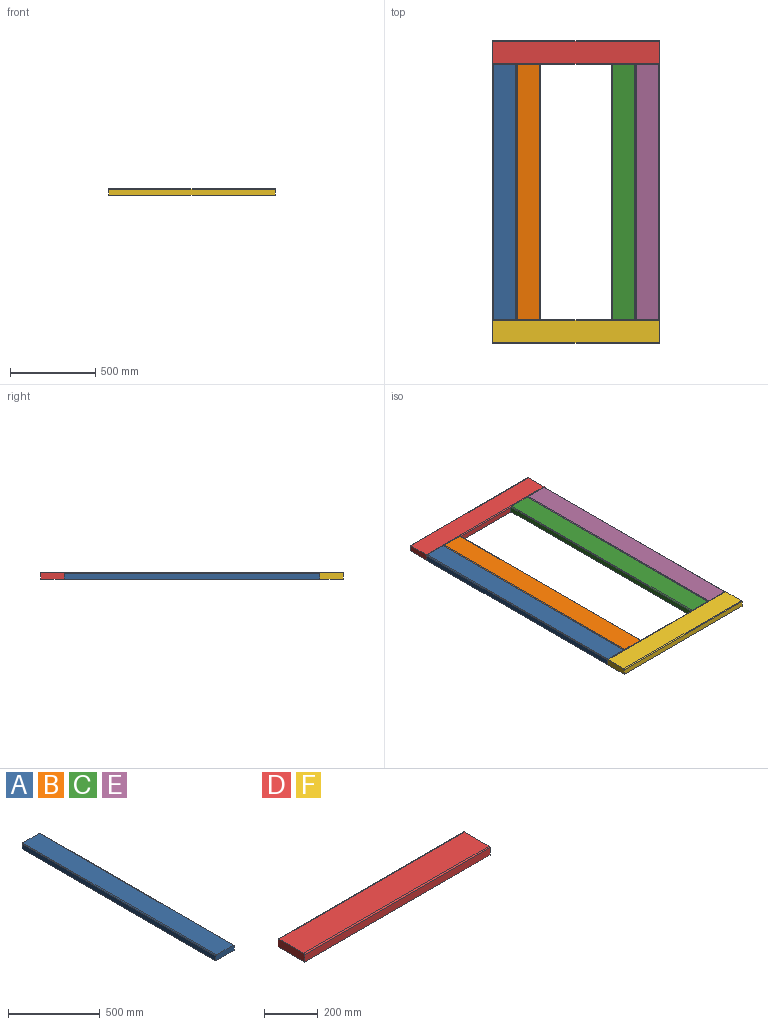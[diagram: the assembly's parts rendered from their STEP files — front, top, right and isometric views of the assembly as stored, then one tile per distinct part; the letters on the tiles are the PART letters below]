
ASSEMBLY  parts=6 mates=15
PART A: 8 faces, bbox 139.7x1498.6x38.1 mm
  f0: plane 1498.6x33.02mm, normal (-1,0,0), area 49483.8mm2, adj f1,f3,f5,f7
  f1: plane 139.7x38.1mm, normal (0,-1,0), area 5311.5mm2, adj f0,f2,f4,f5,f6,f7
  f2: plane 1498.6x33.02mm, normal (1,0,0), area 49483.8mm2, adj f1,f3,f5,f6
  f3: plane 139.7x38.1mm, normal (0,1,0), area 5311.5mm2, adj f0,f2,f4,f5,f6,f7
  f4: plane 1498.6x129.54mm, normal (0,0,1), area 194128.6mm2, adj f1,f3,f6,f7
  f5: plane 1498.6x139.7mm, normal (0,0,-1), area 209354.4mm2, adj f0,f1,f2,f3
  f6: cylinder r=5.08mm len=1498.6mm, axis (0,-1,0), area 11958.3mm2, adj f1,f2,f3,f4
  f7: cylinder r=5.08mm len=1498.6mm, axis (0,1,0), area 11958.3mm2, adj f0,f1,f3,f4
PART B: same geometry as A
PART C: same geometry as A
PART D: 8 faces, bbox 977.9x139.7x38.1 mm
  f0: plane 977.9x33.02mm, normal (0,-1,0), area 32290.3mm2, adj f1,f3,f5,f7
  f1: plane 139.7x38.1mm, normal (1,0,0), area 5311.5mm2, adj f0,f2,f4,f5,f6,f7
  f2: plane 977.9x33.02mm, normal (0,1,0), area 32290.3mm2, adj f1,f3,f5,f6
  f3: plane 139.7x38.1mm, normal (-1,0,0), area 5311.5mm2, adj f0,f2,f4,f5,f6,f7
  f4: plane 977.9x129.54mm, normal (0,0,1), area 126677.2mm2, adj f1,f3,f6,f7
  f5: plane 977.9x139.7mm, normal (0,0,-1), area 136612.6mm2, adj f0,f1,f2,f3
  f6: cylinder r=5.08mm len=977.9mm, axis (1,0,0), area 7803.3mm2, adj f1,f2,f3,f4
  f7: cylinder r=5.08mm len=977.9mm, axis (-1,0,0), area 7803.3mm2, adj f0,f1,f3,f4
PART E: same geometry as A
PART F: same geometry as D
PLACE A t=(-1939.83,412.02,-140.4)mm
PLACE B t=(-1800.13,412.02,-140.4)mm
PLACE C t=(-1241.33,412.02,-140.4)mm
PLACE D t=(-961.93,1910.62,-140.4)mm
PLACE E t=(-1101.63,412.02,-140.4)mm fixed
PLACE F t=(-961.93,272.32,-140.4)mm
MATE planar B.f0 <-> A.f2  axis (-1,0,0) through (-1800.13,1161.32,-123.89)mm
MATE planar C.f1 <-> F.f2  axis (0,-1,0) through (-1171.48,412.02,-121.38)mm
MATE planar E.f5 <-> F.f5  axis (0,0,-1) through (-1101.63,412.02,-140.4)mm
MATE planar C.f4 <-> F.f4  axis (0,0,1) through (-1171.48,1161.32,-102.3)mm
MATE planar F.f1 <-> E.f2  axis (1,0,0) through (-961.93,342.17,-121.38)mm
MATE planar A.f3 <-> D.f0  axis (0,1,0) through (-1869.98,1910.62,-121.38)mm
MATE planar D.f3 <-> A.f0  axis (-1,0,0) through (-1939.83,1980.47,-121.38)mm
MATE planar A.f5 <-> D.f5  axis (0,0,-1) through (-1869.98,1161.32,-140.4)mm
MATE planar B.f4 <-> F.f4  axis (0,0,1) through (-1730.28,1161.32,-102.3)mm
MATE planar C.f2 <-> E.f0  axis (1,0,0) through (-1101.63,1161.32,-123.89)mm
MATE planar F.f2 <-> B.f1  axis (0,1,0) through (-1450.88,412.02,-123.89)mm
MATE planar D.f5 <-> E.f5  axis (0,0,-1) through (-1450.88,1980.47,-140.4)mm
MATE planar E.f3 <-> D.f0  axis (0,1,0) through (-1031.78,1910.62,-121.38)mm
MATE planar E.f1 <-> F.f2  axis (0,-1,0) through (-1031.78,412.02,-121.38)mm
MATE planar E.f2 <-> D.f1  axis (1,0,0) through (-961.93,1161.32,-123.89)mm
